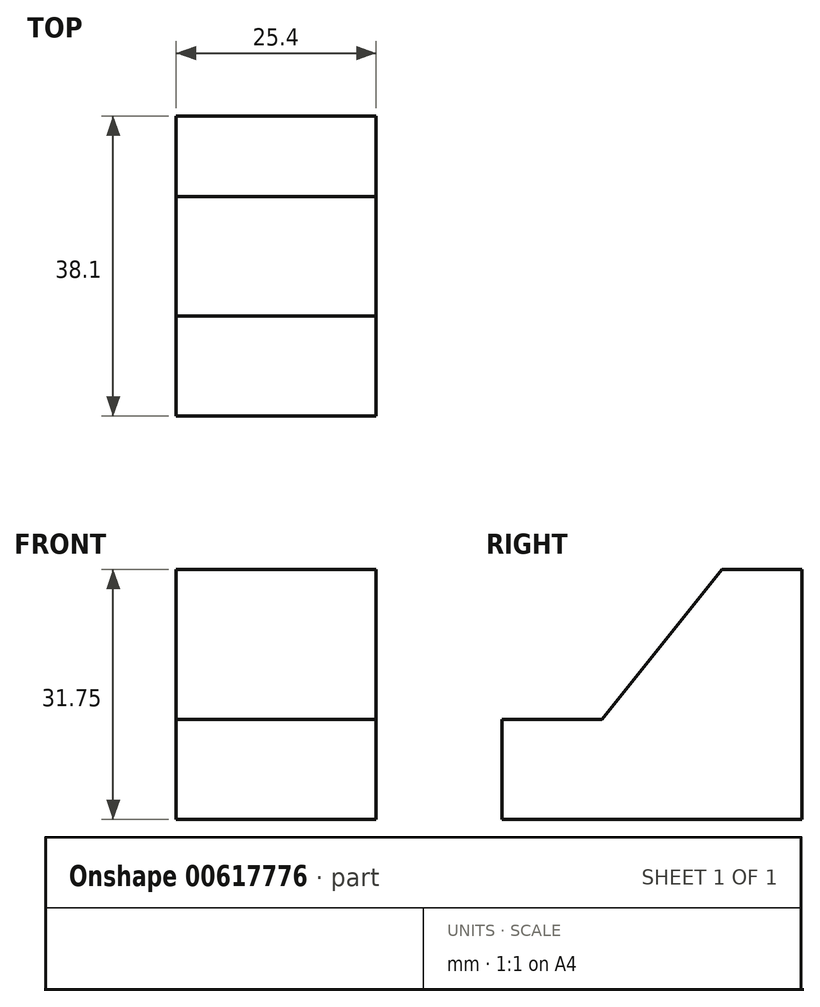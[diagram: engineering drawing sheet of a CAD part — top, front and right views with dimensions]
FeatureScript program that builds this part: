
annotation { "Feature Type Name" : "Feature", "Feature Type Description" : "" }
export const myFeature = defineFeature(function(context is Context, id is Id, definition is map)
    precondition{}
    {
        {
            var Q0;
            Q0=qCreatedBy(makeId("Right.planeOp"),FACE);
            var sketch = newSketch(context, id + "F0", { "sketchPlane" : qUnion([Q0])});
            skLineSegment(sketch, "E0", {"start": v(0, 31.75) * mm, "end": v(0, 0) * mm});
            skLineSegment(sketch, "E1", {"start": v(0, 0) * mm, "end": v(-38.1, 0) * mm});
            skLineSegment(sketch, "E2", {"start": v(-38.1, 0) * mm, "end": v(-38.1, 12.7) * mm});
            skLineSegment(sketch, "E3", {"start": v(-38.1, 12.7) * mm, "end": v(-25.4, 12.7) * mm});
            skLineSegment(sketch, "E4", {"start": v(-25.4, 12.7) * mm, "end": v(-10.2, 31.75) * mm});
            skLineSegment(sketch, "E5", {"start": v(-10.2, 31.75) * mm, "end": v(0, 31.75) * mm});
            skSolve(sketch);
        }
        {
            var Q0;
            Q0 = qSketchRegion(id + "F0", true);
            extrude(context, id + "F1", {"entities" : qUnion([Q0]), "depth" : 25.4 * mm, "offsetDistance" : 25.4 * mm});
        }
    });
